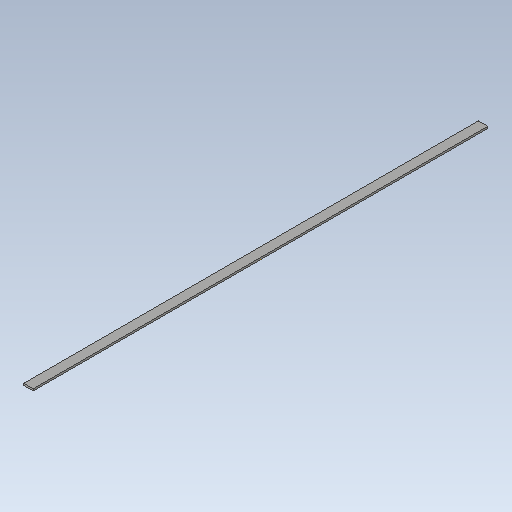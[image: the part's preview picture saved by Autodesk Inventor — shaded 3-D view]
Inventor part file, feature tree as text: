
AUTODESK INVENTOR PART (.ipt)
format: ipt  version: 2020.1 (Build 241239000, 239)  size: 110,592 bytes
history: native  units: mm
features: extrude x1, other x1, sketch x1
ambient origin geometry x8: Origin, YZ Plane, XZ Plane, XY Plane, X Axis, Y Axis, Z Axis, Center Point
bodies: Solid1 (feature_tree)
feature tree (3):
  extrude  "Extrusion1"  Depth=5.0mm
  other  "Work Axis1"
  sketch  "Sketch1"  dims[d0=25.0mm d1=5.0mm d2=1208.95mm d3=0.0mm]
